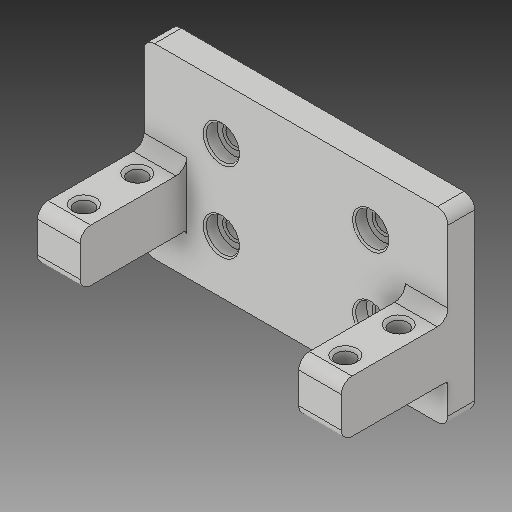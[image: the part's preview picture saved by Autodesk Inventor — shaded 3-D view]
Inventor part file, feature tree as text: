
AUTODESK INVENTOR PART (.ipt)
format: ipt  version: 2019 (Build 230136000, 136)  size: 274,432 bytes
history: native  units: mm
features: extrude x4, fillet x4, sketch x4, chamfer x2, thicken_offset x2
ambient origin geometry x8: Origin, YZ Plane, XZ Plane, XY Plane, X Axis, Y Axis, Z Axis, Center Point
bodies: Solid1 (feature_tree)
feature tree (16):
  extrude  "Extrusion1"  Depth=15.0mm
  extrude  "Extrusion2"  Depth=35.0mm
  extrude  "Extrusion4"  Depth=5.0mm
  fillet  "Fillet2"  Radius=3.5mm
  fillet  "Fillet3"  Radius=3.5mm
  fillet  "Fillet4"  Radius=5.0mm
  chamfer  "Chamfer1"  Distance=20.5mm
  chamfer  "Chamfer2"  Distance=7.0mm
  extrude  "Extrusion5"  Depth=9.8mm
  fillet  "Fillet5"  Radius=20.0mm
  thicken_offset  "Thicken1"
  thicken_offset  "Thicken2"
  sketch  "Sketch1"  dims[d0=28.0mm d1=15.0mm]
  sketch  "Sketch2"  dims[d2=55.0mm d3=35.0mm]
  sketch  "Sketch4"  dims[d4=3.5mm d5=3.5mm d6=3.5mm d7=3.5mm d8=5.0mm d9=0.0mm]
  sketch  "Sketch5"  dims[d10=10.0mm d11=20.5mm d12=7.0mm d13=9.8mm d14=20.0mm d15=0.0mm d26=24.5mm d27=10.25mm d28=3.4mm d29=10.0mm d30=90.0deg d31=3.4mm d32=10.0mm d33=0.0mm d34=2.0mm d35=0.5mm d36=2.0mm d37=0.5mm d38=2.0mm d39=45.0deg d40=0.5mm d41=2.0mm d42=45.0deg d46=6.2mm d47=6.2mm d48=6.2mm d49=6.2mm d50=2.3mm d51=0.0mm d52=0.3mm d53=1.0mm d54=1.0mm d55=1.0mm d56=1.0mm]
